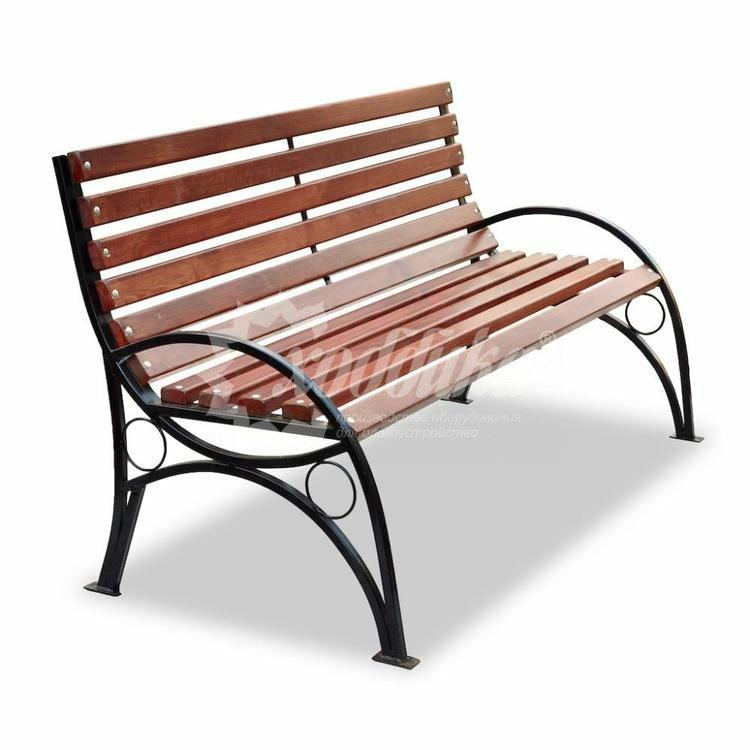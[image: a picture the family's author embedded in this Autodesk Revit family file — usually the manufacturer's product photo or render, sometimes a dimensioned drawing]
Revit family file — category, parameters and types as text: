
# Revit family: Скамейка стальная «Бульвар» Арт 7055
name_source: partatom
category: Антураж
revit_build: Autodesk Revit 2018 (Build: 20180423_1000(x64)
units: mm (PartAtom-declared; Revit-internal decimal feet)

## family parameters
Всегда вертикально = Да
Источник визуального образа = Геометрия семейства
На основе рабочей плоскости = Нет
Общий = Нет
При загрузке вырезать с полостями = Нет
Точка расчета площади = Нет

## types (7) — shared parameters
URL = https://hobbyka.ru
Артикул товара = Арт. 7055
Высота = 840 мм
Группа модели = Садовые скамейки
Изготовитель = ООО «Хоббика»
Изображение типоразмера = Скамейка стальная «Бульвар» Арт 7055.jpg
Материал изделия = Сталь, дерево
Цвет опоры = Сталь
Цвет сидения = Дерево
Ширина = 760 мм

## per-type parameters (varying)
| type | Версия 0,6 м (кресло) | Версия 1,2 м | Версия 1,5 м | Версия 1,8 м | Версия 2,0 м (2 опоры) | Версия 2,0 м (3 опоры) | Версия 3,0 м (3 опоры) | Длина | Описание | Средняя опора |
| Версия 0,6 м (кресло) | Да | Нет | Нет | Нет | Нет | Нет | Нет | 640 мм | Скамейка стальная «Бульвар». Версия 0,6 м (кресло) | Нет |
| Версия 1,2 м | Нет | Да | Нет | Нет | Нет | Нет | Нет | 1240 мм | Скамейка стальная «Бульвар». Версия 1,2 м | Нет |
| Версия 1,5 м | Нет | Нет | Да | Нет | Нет | Нет | Нет | 1540 мм | Скамейка стальная «Бульвар». Версия 1,5 м | Нет |
| Версия 1,8 м | Нет | Нет | Нет | Да | Нет | Нет | Нет | 1840 мм | Скамейка стальная «Бульвар». Версия 1,8 м | Нет |
| Версия 2,0 м (2 опоры) | Нет | Нет | Нет | Нет | Да | Нет | Нет | 2040 мм | Скамейка стальная «Бульвар». Версия 2,0 м (2 опоры) | Нет |
| Версия 2,0 м (3 опоры) | Нет | Нет | Нет | Нет | Нет | Да | Нет | 2040 мм | Скамейка стальная «Бульвар». Версия 2,0 м (3 опоры) | Да |
| Версия 3,0 м (3 опоры) | Нет | Нет | Нет | Нет | Нет | Нет | Да | 3040 мм | Скамейка стальная «Бульвар». Версия 3,0 м (3 опоры) | Да |
